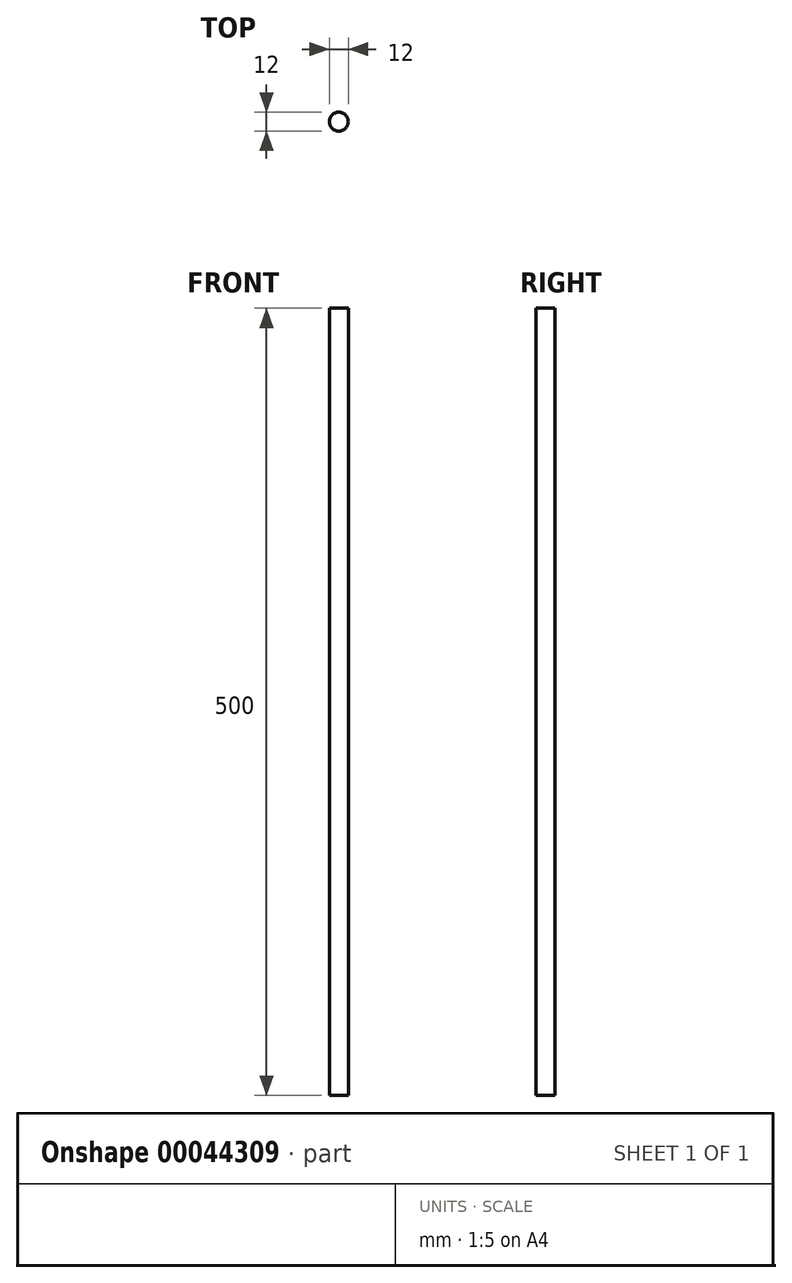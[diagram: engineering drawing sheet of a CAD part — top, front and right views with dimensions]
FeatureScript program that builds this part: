
annotation { "Feature Type Name" : "Feature", "Feature Type Description" : "" }
export const myFeature = defineFeature(function(context is Context, id is Id, definition is map)
    precondition{}
    {
        {
            var Q0;
            Q0=qCreatedBy(makeId("Top.planeOp"),FACE);
            var sketch = newSketch(context, id + "F0", { "sketchPlane" : qUnion([Q0])});
            skCircle(sketch, "E0", {"center": v(0, 0) * mm, "radius": 6 * mm});
            skSolve(sketch);
        }
        {
            var Q0;
            Q0 = qSketchRegion(id + "F0", true);
            extrude(context, id + "F1", {"entities" : qUnion([Q0]), "depth" : 500 * mm});
        }
    });
